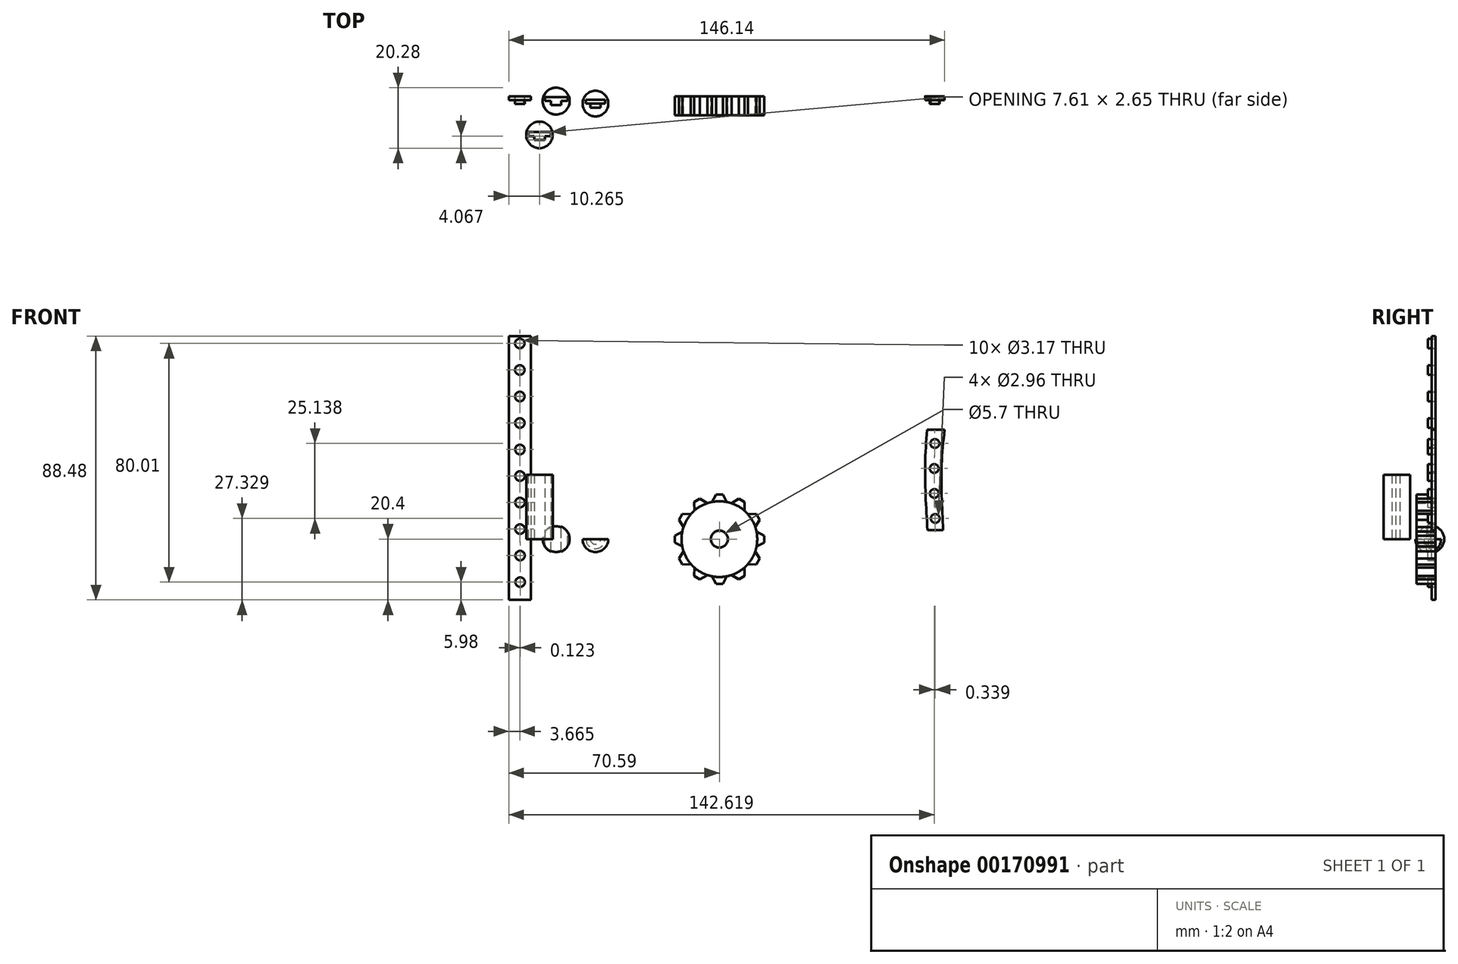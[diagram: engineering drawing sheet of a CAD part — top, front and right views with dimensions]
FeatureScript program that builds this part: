
annotation { "Feature Type Name" : "Feature", "Feature Type Description" : "" }
export const myFeature = defineFeature(function(context is Context, id is Id, definition is map)
    precondition{}
    {
        {
            var Q0;
            Q0=qCreatedBy(makeId("Front.planeOp"),FACE);
            var sketch = newSketch(context, id + "F0", { "sketchPlane" : qUnion([Q0])});
            skLineSegment(sketch, "E0", {"start": v(1.15, 14.98) * mm, "end": v(2.48, 12.45) * mm});
            skLineSegment(sketch, "E1.MirrorCS", {"start": v(-1.15, 14.98) * mm, "end": v(-2.48, 12.45) * mm});
            skLineSegment(sketch, "E2", {"start": v(-1.15, 14.98) * mm, "end": v(1.15, 14.98) * mm});
            skCircle(sketch, "E3", {"center": v(0, 0) * mm, "radius": 2.85 * mm});
            skCircle(sketch, "E4", {"center": v(0, 0) * mm, "radius": 12.7 * mm});
            skLineSegment(sketch, "E5.1.0", {"start": v(-6.5, 13.54) * mm, "end": v(-4.08, 12.03) * mm});
            skLineSegment(sketch, "E5.1.1", {"start": v(-8.48, 12.4) * mm, "end": v(-8.38, 9.54) * mm});
            skLineSegment(sketch, "E5.1.2", {"start": v(-8.48, 12.4) * mm, "end": v(-6.5, 13.54) * mm});
            skLineSegment(sketch, "E5.2.0", {"start": v(-12.4, 8.48) * mm, "end": v(-9.54, 8.38) * mm});
            skLineSegment(sketch, "E5.2.1", {"start": v(-13.54, 6.5) * mm, "end": v(-12.03, 4.08) * mm});
            skLineSegment(sketch, "E5.2.2", {"start": v(-13.54, 6.5) * mm, "end": v(-12.4, 8.48) * mm});
            skLineSegment(sketch, "E5.3.0", {"start": v(-14.98, 1.15) * mm, "end": v(-12.45, 2.48) * mm});
            skLineSegment(sketch, "E5.3.1", {"start": v(-14.98, -1.15) * mm, "end": v(-12.45, -2.48) * mm});
            skLineSegment(sketch, "E5.3.2", {"start": v(-14.98, -1.15) * mm, "end": v(-14.98, 1.15) * mm});
            skLineSegment(sketch, "E5.4.0", {"start": v(-13.54, -6.5) * mm, "end": v(-12.03, -4.08) * mm});
            skLineSegment(sketch, "E5.4.1", {"start": v(-12.4, -8.48) * mm, "end": v(-9.54, -8.38) * mm});
            skLineSegment(sketch, "E5.4.2", {"start": v(-12.4, -8.48) * mm, "end": v(-13.54, -6.5) * mm});
            skLineSegment(sketch, "E5.5.0", {"start": v(-8.48, -12.4) * mm, "end": v(-8.38, -9.54) * mm});
            skLineSegment(sketch, "E5.5.1", {"start": v(-6.5, -13.54) * mm, "end": v(-4.08, -12.03) * mm});
            skLineSegment(sketch, "E5.5.2", {"start": v(-6.5, -13.54) * mm, "end": v(-8.48, -12.4) * mm});
            skLineSegment(sketch, "E5.6.0", {"start": v(-1.15, -14.98) * mm, "end": v(-2.48, -12.45) * mm});
            skLineSegment(sketch, "E5.6.1", {"start": v(1.15, -14.98) * mm, "end": v(2.48, -12.45) * mm});
            skLineSegment(sketch, "E5.6.2", {"start": v(1.15, -14.98) * mm, "end": v(-1.15, -14.98) * mm});
            skLineSegment(sketch, "E5.7.0", {"start": v(6.5, -13.54) * mm, "end": v(4.08, -12.03) * mm});
            skLineSegment(sketch, "E5.7.1", {"start": v(8.48, -12.4) * mm, "end": v(8.38, -9.54) * mm});
            skLineSegment(sketch, "E5.7.2", {"start": v(8.48, -12.4) * mm, "end": v(6.5, -13.54) * mm});
            skLineSegment(sketch, "E5.8.0", {"start": v(12.4, -8.48) * mm, "end": v(9.54, -8.38) * mm});
            skLineSegment(sketch, "E5.8.1", {"start": v(13.54, -6.5) * mm, "end": v(12.03, -4.08) * mm});
            skLineSegment(sketch, "E5.8.2", {"start": v(13.54, -6.5) * mm, "end": v(12.4, -8.48) * mm});
            skLineSegment(sketch, "E5.9.0", {"start": v(14.98, -1.15) * mm, "end": v(12.45, -2.48) * mm});
            skLineSegment(sketch, "E5.9.1", {"start": v(14.98, 1.15) * mm, "end": v(12.45, 2.48) * mm});
            skLineSegment(sketch, "E5.9.2", {"start": v(14.98, 1.15) * mm, "end": v(14.98, -1.15) * mm});
            skLineSegment(sketch, "E5.10.0", {"start": v(13.54, 6.5) * mm, "end": v(12.03, 4.08) * mm});
            skLineSegment(sketch, "E5.10.1", {"start": v(12.4, 8.48) * mm, "end": v(9.54, 8.38) * mm});
            skLineSegment(sketch, "E5.10.2", {"start": v(12.4, 8.48) * mm, "end": v(13.54, 6.5) * mm});
            skLineSegment(sketch, "E5.11.0", {"start": v(8.48, 12.4) * mm, "end": v(8.38, 9.54) * mm});
            skLineSegment(sketch, "E5.11.1", {"start": v(6.5, 13.54) * mm, "end": v(4.08, 12.03) * mm});
            skLineSegment(sketch, "E5.11.2", {"start": v(6.5, 13.54) * mm, "end": v(8.48, 12.4) * mm});
            skLineSegment(sketch, "E6.bottom", {"start": v(48.7, 52.46) * mm, "end": v(58.15, 52.46) * mm});
            skLineSegment(sketch, "E6.top", {"start": v(48.7, 3.3) * mm, "end": v(58.15, 3.3) * mm});
            skLineSegment(sketch, "E6.left", {"start": v(48.7, 52.46) * mm, "end": v(48.7, 3.3) * mm});
            skLineSegment(sketch, "E6.right", {"start": v(58.15, 52.46) * mm, "end": v(58.15, 3.3) * mm});
            skLineSegment(sketch, "E7", {"start": v(53.43, 3.3) * mm, "end": v(53.43, 6.13) * mm});
            skCircle(sketch, "E8", {"center": v(53.43, 6.13) * mm, "radius": 1.38 * mm});
            skFitSpline(sketch, "E9", {"points": [v(69.76, 3.01) * mm, v(69.06, 27.56) * mm, v(71.5, 52.14) * mm], "startDerivative": vector(-2.96, 49.08) * mm, "endDerivative": vector(6.45, 48.4) * mm});
            skFitSpline(sketch, "E10", {"points": [v(74.98, 3.01) * mm, v(74.63, 27.56) * mm, v(77.4, 52.14) * mm], "startDerivative": vector(-1.57, 49.03) * mm, "endDerivative": vector(3.66, 48.45) * mm});
            skLineSegment(sketch, "E11", {"start": v(69.76, 3.01) * mm, "end": v(74.98, 3.01) * mm});
            skCircle(sketch, "E12", {"center": v(72.37, 6.93) * mm, "radius": 1.48 * mm});
            skPoint(sketch, "E12.centerSnap0", {"position": v(72.37, 3.01) * mm});
            skCircle(sketch, "E13.1.0.0", {"center": v(72.07, 15.3) * mm, "radius": 1.48 * mm});
            skCircle(sketch, "E13.2.0.0", {"center": v(72.03, 23.69) * mm, "radius": 1.48 * mm});
            skCircle(sketch, "E13.3.0.0", {"center": v(72.24, 32.07) * mm, "radius": 1.48 * mm});
            skLineSegment(sketch, "E14", {"start": v(69.66, 36.67) * mm, "end": v(75.55, 36.67) * mm});
            skLineSegment(sketch, "E15.bottom", {"start": v(-70.59, 68.08) * mm, "end": v(-63.26, 68.08) * mm});
            skLineSegment(sketch, "E15.top", {"start": v(-70.59, -20.4) * mm, "end": v(-63.26, -20.4) * mm});
            skLineSegment(sketch, "E15.left", {"start": v(-70.59, 68.08) * mm, "end": v(-70.59, -20.4) * mm});
            skLineSegment(sketch, "E15.right", {"start": v(-63.26, 68.08) * mm, "end": v(-63.26, -20.4) * mm});
            skCircle(sketch, "E16", {"center": v(-66.92, 65.6) * mm, "radius": 1.59 * mm});
            skPoint(sketch, "E16.centerSnap0", {"position": v(-66.92, 68.08) * mm});
            skPoint(sketch, "E17.centerSnap0", {"position": v(-66.92, -20.4) * mm});
            skCircle(sketch, "E18.1.0.0", {"center": v(-66.91, 56.7) * mm, "radius": 1.59 * mm});
            skCircle(sketch, "E18.2.0.0", {"center": v(-66.9, 47.81) * mm, "radius": 1.59 * mm});
            skCircle(sketch, "E18.3.0.0", {"center": v(-66.88, 38.92) * mm, "radius": 1.59 * mm});
            skCircle(sketch, "E18.4.0.0", {"center": v(-66.87, 30.03) * mm, "radius": 1.59 * mm});
            skCircle(sketch, "E18.5.0.0", {"center": v(-66.86, 21.14) * mm, "radius": 1.59 * mm});
            skCircle(sketch, "E18.6.0.0", {"center": v(-66.84, 12.25) * mm, "radius": 1.59 * mm});
            skCircle(sketch, "E18.7.0.0", {"center": v(-66.83, 3.36) * mm, "radius": 1.59 * mm});
            skCircle(sketch, "E18.8.0.0", {"center": v(-66.82, -5.53) * mm, "radius": 1.59 * mm});
            skCircle(sketch, "E18.9.0.0", {"center": v(-66.8, -14.42) * mm, "radius": 1.59 * mm});
            skSolve(sketch);
        }
        {
            var Q0;
            Q0=makeQuery(id+"F0.imprint","IMPRINT",FACE,{"disambiguationData":[TD([[makeQuery(id+"F0.imprint","IMPRINT",EDGE,{"derivedFrom":sQuery(id+"F0.wireOp",EDGE,"9e9577b3-fb2f-4fc8-aa35-3dcf2ef7b522")}),-1.0]])]});
            var Q1;
            {var subQ0=sQuery(id+"F0.wireOp",EDGE,"E5.10.0");Q1=makeQuery(id+"F0.imprint","IMPRINT",FACE,{"disambiguationData":[TD([[makeQuery(id+"F0.imprint","IMPRINT",EDGE,{"derivedFrom":subQ0}),-1.0]])]});}
            var Q2;
            {var subQ0=sQuery(id+"F0.wireOp",EDGE,"E5.11.0");Q2=makeQuery(id+"F0.imprint","IMPRINT",FACE,{"disambiguationData":[TD([[makeQuery(id+"F0.imprint","IMPRINT",EDGE,{"derivedFrom":subQ0}),-1.0]])]});}
            var Q3;
            {var subQ0=sQuery(id+"F0.wireOp",EDGE,"E5.2.0");Q3=makeQuery(id+"F0.imprint","IMPRINT",FACE,{"disambiguationData":[TD([[makeQuery(id+"F0.imprint","IMPRINT",EDGE,{"derivedFrom":subQ0}),-1.0]])]});}
            var Q4;
            {var subQ0=sQuery(id+"F0.wireOp",EDGE,"E5.3.0");Q4=makeQuery(id+"F0.imprint","IMPRINT",FACE,{"disambiguationData":[TD([[makeQuery(id+"F0.imprint","IMPRINT",EDGE,{"derivedFrom":subQ0}),-1.0]])]});}
            var Q5;
            {var subQ0=sQuery(id+"F0.wireOp",EDGE,"E5.4.0");Q5=makeQuery(id+"F0.imprint","IMPRINT",FACE,{"disambiguationData":[TD([[makeQuery(id+"F0.imprint","IMPRINT",EDGE,{"derivedFrom":subQ0}),-1.0]])]});}
            var Q6;
            {var subQ0=sQuery(id+"F0.wireOp",EDGE,"E5.5.0");Q6=makeQuery(id+"F0.imprint","IMPRINT",FACE,{"disambiguationData":[TD([[makeQuery(id+"F0.imprint","IMPRINT",EDGE,{"derivedFrom":subQ0}),-1.0]])]});}
            var Q7;
            {var subQ0=sQuery(id+"F0.wireOp",EDGE,"E5.6.0");Q7=makeQuery(id+"F0.imprint","IMPRINT",FACE,{"disambiguationData":[TD([[makeQuery(id+"F0.imprint","IMPRINT",EDGE,{"derivedFrom":subQ0}),-1.0]])]});}
            var Q8;
            {var subQ0=sQuery(id+"F0.wireOp",EDGE,"E5.7.0");Q8=makeQuery(id+"F0.imprint","IMPRINT",FACE,{"disambiguationData":[TD([[makeQuery(id+"F0.imprint","IMPRINT",EDGE,{"derivedFrom":subQ0}),-1.0]])]});}
            var Q9;
            {var subQ0=sQuery(id+"F0.wireOp",EDGE,"E5.8.0");Q9=makeQuery(id+"F0.imprint","IMPRINT",FACE,{"disambiguationData":[TD([[makeQuery(id+"F0.imprint","IMPRINT",EDGE,{"derivedFrom":subQ0}),-1.0]])]});}
            var Q10;
            {var subQ0=sQuery(id+"F0.wireOp",EDGE,"E5.9.0");Q10=makeQuery(id+"F0.imprint","IMPRINT",FACE,{"disambiguationData":[TD([[makeQuery(id+"F0.imprint","IMPRINT",EDGE,{"derivedFrom":subQ0}),-1.0]])]});}
            var Q11;
            {var subQ0=sQuery(id+"F0.wireOp",EDGE,"E0");Q11=makeQuery(id+"F0.imprint","IMPRINT",FACE,{"disambiguationData":[TD([[makeQuery(id+"F0.imprint","IMPRINT",EDGE,{"derivedFrom":subQ0}),-1.0]])]});}
            var Q12;
            {var subQ0=sQuery(id+"F0.wireOp",EDGE,"E5.1.0");Q12=makeQuery(id+"F0.imprint","IMPRINT",FACE,{"disambiguationData":[TD([[makeQuery(id+"F0.imprint","IMPRINT",EDGE,{"derivedFrom":subQ0}),-1.0]])]});}
            extrude(context, id + "F1", {"entities" : qUnion([Q0, Q1, Q2, Q3, Q4, Q5, Q6, Q7, Q8, Q9, Q10, Q11, Q12]), "depth" : 6.35 * mm});
        }
        {
            var Q0;
            Q0=makeQuery(id+"F0.imprint","IMPRINT",FACE,{"disambiguationData":[TD([[makeQuery(id+"F0.imprint","IMPRINT",EDGE,{"derivedFrom":sQuery(id+"F0.wireOp",EDGE,"9e9577b3-fb2f-4fc8-aa35-3dcf2ef7b522")}),-1.0]])]});
            var Q1;
            {var subQ0=sQuery(id+"F0.wireOp",EDGE,"E0");Q1=makeQuery(id+"F0.imprint","IMPRINT",FACE,{"disambiguationData":[TD([[makeQuery(id+"F0.imprint","IMPRINT",EDGE,{"derivedFrom":subQ0}),-1.0]])]});}
            var Q2;
            {var subQ0=sQuery(id+"F0.wireOp",EDGE,"E5.10.0");Q2=makeQuery(id+"F0.imprint","IMPRINT",FACE,{"disambiguationData":[TD([[makeQuery(id+"F0.imprint","IMPRINT",EDGE,{"derivedFrom":subQ0}),-1.0]])]});}
            var Q3;
            {var subQ0=sQuery(id+"F0.wireOp",EDGE,"E5.11.0");Q3=makeQuery(id+"F0.imprint","IMPRINT",FACE,{"disambiguationData":[TD([[makeQuery(id+"F0.imprint","IMPRINT",EDGE,{"derivedFrom":subQ0}),-1.0]])]});}
            var Q4;
            {var subQ0=sQuery(id+"F0.wireOp",EDGE,"E5.1.0");Q4=makeQuery(id+"F0.imprint","IMPRINT",FACE,{"disambiguationData":[TD([[makeQuery(id+"F0.imprint","IMPRINT",EDGE,{"derivedFrom":subQ0}),-1.0]])]});}
            var Q5;
            {var subQ0=sQuery(id+"F0.wireOp",EDGE,"E5.2.0");Q5=makeQuery(id+"F0.imprint","IMPRINT",FACE,{"disambiguationData":[TD([[makeQuery(id+"F0.imprint","IMPRINT",EDGE,{"derivedFrom":subQ0}),-1.0]])]});}
            var Q6;
            {var subQ0=sQuery(id+"F0.wireOp",EDGE,"E5.3.0");Q6=makeQuery(id+"F0.imprint","IMPRINT",FACE,{"disambiguationData":[TD([[makeQuery(id+"F0.imprint","IMPRINT",EDGE,{"derivedFrom":subQ0}),-1.0]])]});}
            var Q7;
            {var subQ0=sQuery(id+"F0.wireOp",EDGE,"E5.4.0");Q7=makeQuery(id+"F0.imprint","IMPRINT",FACE,{"disambiguationData":[TD([[makeQuery(id+"F0.imprint","IMPRINT",EDGE,{"derivedFrom":subQ0}),-1.0]])]});}
            var Q8;
            {var subQ0=sQuery(id+"F0.wireOp",EDGE,"E5.5.0");Q8=makeQuery(id+"F0.imprint","IMPRINT",FACE,{"disambiguationData":[TD([[makeQuery(id+"F0.imprint","IMPRINT",EDGE,{"derivedFrom":subQ0}),-1.0]])]});}
            var Q9;
            {var subQ0=sQuery(id+"F0.wireOp",EDGE,"E5.6.0");Q9=makeQuery(id+"F0.imprint","IMPRINT",FACE,{"disambiguationData":[TD([[makeQuery(id+"F0.imprint","IMPRINT",EDGE,{"derivedFrom":subQ0}),-1.0]])]});}
            var Q10;
            {var subQ0=sQuery(id+"F0.wireOp",EDGE,"E5.7.0");Q10=makeQuery(id+"F0.imprint","IMPRINT",FACE,{"disambiguationData":[TD([[makeQuery(id+"F0.imprint","IMPRINT",EDGE,{"derivedFrom":subQ0}),-1.0]])]});}
            var Q11;
            {var subQ0=sQuery(id+"F0.wireOp",EDGE,"E5.8.0");Q11=makeQuery(id+"F0.imprint","IMPRINT",FACE,{"disambiguationData":[TD([[makeQuery(id+"F0.imprint","IMPRINT",EDGE,{"derivedFrom":subQ0}),-1.0]])]});}
            var Q12;
            {var subQ0=sQuery(id+"F0.wireOp",EDGE,"E5.9.0");Q12=makeQuery(id+"F0.imprint","IMPRINT",FACE,{"disambiguationData":[TD([[makeQuery(id+"F0.imprint","IMPRINT",EDGE,{"derivedFrom":subQ0}),-1.0]])]});}
            var Q13;
            Q13=makeQuery(id+"F0.imprint","IMPRINT",FACE,{"disambiguationData":[TD([[makeQuery(id+"F0.imprint","IMPRINT",EDGE,{"derivedFrom":sQuery(id+"F0.wireOp",EDGE,"E3")}),-1.0]])]});
            extrude(context, id + "F2", {"entities" : qUnion([Q0, Q1, Q2, Q3, Q4, Q5, Q6, Q7, Q8, Q9, Q10, Q11, Q12, Q13]), "depth" : 6.35 * mm});
        }
        {
            var Q0;
            Q0=makeQuery(id+"F0.imprint","IMPRINT",FACE,{"disambiguationData":[TD([[makeQuery(id+"F0.imprint","IMPRINT",EDGE,{"derivedFrom":sQuery(id+"F0.wireOp",EDGE,"E13.5.0.0")}),1.0]])]});
            var Q1;
            Q1=makeQuery(id+"F0.imprint","IMPRINT",FACE,{"disambiguationData":[TD([[makeQuery(id+"F0.imprint","IMPRINT",EDGE,{"derivedFrom":sQuery(id+"F0.wireOp",EDGE,"E13.4.0.0")}),1.0]])]});
            var Q2;
            Q2=makeQuery(id+"F0.imprint","IMPRINT",FACE,{"disambiguationData":[TD([[makeQuery(id+"F0.imprint","IMPRINT",EDGE,{"derivedFrom":sQuery(id+"F0.wireOp",EDGE,"E13.3.0.0")}),1.0]])]});
            var Q3;
            Q3=makeQuery(id+"F0.imprint","IMPRINT",FACE,{"disambiguationData":[TD([[makeQuery(id+"F0.imprint","IMPRINT",EDGE,{"derivedFrom":sQuery(id+"F0.wireOp",EDGE,"E13.2.0.0")}),1.0]])]});
            var Q4;
            Q4=makeQuery(id+"F0.imprint","IMPRINT",FACE,{"disambiguationData":[TD([[makeQuery(id+"F0.imprint","IMPRINT",EDGE,{"derivedFrom":sQuery(id+"F0.wireOp",EDGE,"E13.1.0.0")}),1.0]])]});
            var Q5;
            Q5=makeQuery(id+"F0.imprint","IMPRINT",FACE,{"disambiguationData":[TD([[makeQuery(id+"F0.imprint","IMPRINT",EDGE,{"derivedFrom":sQuery(id+"F0.wireOp",EDGE,"E12")}),1.0]])]});
            extrude(context, id + "F3", {"entities" : qUnion([Q0, Q1, Q2, Q3, Q4, Q5]), "depth" : 2.54 * mm});
        }
        {
            var Q0;
            Q0=makeQuery(id+"F0.imprint","IMPRINT",FACE,{"disambiguationData":[TD([[makeQuery(id+"F0.imprint","IMPRINT",EDGE,{"derivedFrom":sQuery(id+"F0.wireOp",EDGE,"E9")}),-1.0]])]});
            extrude(context, id + "F4", {"entities" : qUnion([Q0]), "depth" : 1.27 * mm});
        }
        {
            var Q0;
            Q0=makeQuery(id+"F0.imprint","IMPRINT",FACE,{"disambiguationData":[TD([[makeQuery(id+"F0.imprint","IMPRINT",EDGE,{"derivedFrom":sQuery(id+"F0.wireOp",EDGE,"E15.bottom")}),-1.0]])]});
            extrude(context, id + "F5", {"entities" : qUnion([Q0]), "depth" : 1.27 * mm});
        }
        {
            var Q0;
            Q0=makeQuery(id+"F0.imprint","IMPRINT",FACE,{"disambiguationData":[TD([[makeQuery(id+"F0.imprint","IMPRINT",EDGE,{"derivedFrom":sQuery(id+"F0.wireOp",EDGE,"E16")}),1.0]])]});
            var Q1;
            Q1=makeQuery(id+"F0.imprint","IMPRINT",FACE,{"disambiguationData":[TD([[makeQuery(id+"F0.imprint","IMPRINT",EDGE,{"derivedFrom":sQuery(id+"F0.wireOp",EDGE,"E18.1.0.0")}),1.0]])]});
            var Q2;
            Q2=makeQuery(id+"F0.imprint","IMPRINT",FACE,{"disambiguationData":[TD([[makeQuery(id+"F0.imprint","IMPRINT",EDGE,{"derivedFrom":sQuery(id+"F0.wireOp",EDGE,"E18.2.0.0")}),1.0]])]});
            var Q3;
            Q3=makeQuery(id+"F0.imprint","IMPRINT",FACE,{"disambiguationData":[TD([[makeQuery(id+"F0.imprint","IMPRINT",EDGE,{"derivedFrom":sQuery(id+"F0.wireOp",EDGE,"E18.3.0.0")}),1.0]])]});
            var Q4;
            Q4=makeQuery(id+"F0.imprint","IMPRINT",FACE,{"disambiguationData":[TD([[makeQuery(id+"F0.imprint","IMPRINT",EDGE,{"derivedFrom":sQuery(id+"F0.wireOp",EDGE,"E18.4.0.0")}),1.0]])]});
            var Q5;
            Q5=makeQuery(id+"F0.imprint","IMPRINT",FACE,{"disambiguationData":[TD([[makeQuery(id+"F0.imprint","IMPRINT",EDGE,{"derivedFrom":sQuery(id+"F0.wireOp",EDGE,"E18.5.0.0")}),1.0]])]});
            var Q6;
            Q6=makeQuery(id+"F0.imprint","IMPRINT",FACE,{"disambiguationData":[TD([[makeQuery(id+"F0.imprint","IMPRINT",EDGE,{"derivedFrom":sQuery(id+"F0.wireOp",EDGE,"E18.6.0.0")}),1.0]])]});
            var Q7;
            Q7=makeQuery(id+"F0.imprint","IMPRINT",FACE,{"disambiguationData":[TD([[makeQuery(id+"F0.imprint","IMPRINT",EDGE,{"derivedFrom":sQuery(id+"F0.wireOp",EDGE,"E18.7.0.0")}),1.0]])]});
            var Q8;
            Q8=makeQuery(id+"F0.imprint","IMPRINT",FACE,{"disambiguationData":[TD([[makeQuery(id+"F0.imprint","IMPRINT",EDGE,{"derivedFrom":sQuery(id+"F0.wireOp",EDGE,"E18.9.0.0")}),1.0]])]});
            var Q9;
            Q9=makeQuery(id+"F0.imprint","IMPRINT",FACE,{"disambiguationData":[TD([[makeQuery(id+"F0.imprint","IMPRINT",EDGE,{"derivedFrom":sQuery(id+"F0.wireOp",EDGE,"E18.8.0.0")}),1.0]])]});
            extrude(context, id + "F6", {"entities" : qUnion([Q0, Q1, Q2, Q3, Q4, Q5, Q6, Q7, Q8, Q9]), "depth" : 2.54 * mm});
        }
        {
            var Q0;
            Q0=qCreatedBy(makeId("Top.planeOp"),FACE);
            var sketch = newSketch(context, id + "F7", { "sketchPlane" : qUnion([Q0])});
            skLineSegment(sketch, "E19", {"start": v(-54.7, -0.24) * mm, "end": v(-58.55, -0.24) * mm});
            skLineSegment(sketch, "E20", {"start": v(-58.55, -1.58) * mm, "end": v(-56.41, -1.58) * mm});
            skLineSegment(sketch, "E21", {"start": v(-56.41, -1.58) * mm, "end": v(-56.41, -2.96) * mm});
            skLineSegment(sketch, "E22", {"start": v(-56.41, -2.96) * mm, "end": v(-54.7, -2.96) * mm});
            skLineSegment(sketch, "E23", {"start": v(-58.55, -0.24) * mm, "end": v(-58.55, -1.58) * mm});
            skArc(sketch, "E24", {"start": v(-54.7, 2.91) * mm, "mid": v(-59.22, -1.6) * mm, "end": v(-54.7, -6.11) * mm});
            skLineSegment(sketch, "E25", {"start": v(-41.54, -1.1) * mm, "end": v(-38.35, -1.1) * mm});
            skLineSegment(sketch, "E26", {"start": v(-38.35, -1.1) * mm, "end": v(-38.35, -2.47) * mm});
            skLineSegment(sketch, "E27", {"start": v(-38.35, -2.47) * mm, "end": v(-39.8, -2.47) * mm});
            skLineSegment(sketch, "E28", {"start": v(-39.8, -2.47) * mm, "end": v(-39.8, -3.84) * mm});
            skLineSegment(sketch, "E29", {"start": v(-39.8, -3.84) * mm, "end": v(-41.54, -3.84) * mm});
            skLineSegment(sketch, "E30", {"start": v(-41.54, 1.85) * mm, "end": v(-41.54, -1.1) * mm});
            skLineSegment(sketch, "E31.trimOffspring", {"start": v(-41.54, -3.84) * mm, "end": v(-41.54, -6.99) * mm});
            skLineSegment(sketch, "E32", {"start": v(-41.54, -7.92) * mm, "end": v(-41.54, 3) * mm, "construction": true});
            skLineSegment(sketch, "E33.MirrorCS", {"start": v(-53, -1.58) * mm, "end": v(-53, -2.96) * mm});
            skLineSegment(sketch, "E34.MirrorCS", {"start": v(-50.86, -0.24) * mm, "end": v(-50.86, -1.58) * mm});
            skLineSegment(sketch, "E35.MirrorCS", {"start": v(-50.86, -1.58) * mm, "end": v(-53, -1.58) * mm});
            skLineSegment(sketch, "E36.MirrorCS", {"start": v(-53, -2.96) * mm, "end": v(-54.7, -2.96) * mm});
            skLineSegment(sketch, "E37.MirrorCS", {"start": v(-54.7, -0.24) * mm, "end": v(-50.86, -0.24) * mm});
            skLineSegment(sketch, "E38", {"start": v(-54.7, 0.25) * mm, "end": v(-54.7, -3.39) * mm, "construction": true});
            skLineSegment(sketch, "E39", {"start": v(-64.13, -11.98) * mm, "end": v(-56.52, -11.98) * mm});
            skLineSegment(sketch, "E40", {"start": v(-56.52, -11.98) * mm, "end": v(-56.52, -13.37) * mm});
            skLineSegment(sketch, "E41", {"start": v(-56.52, -13.37) * mm, "end": v(-58.46, -13.37) * mm});
            skLineSegment(sketch, "E42", {"start": v(-58.46, -13.37) * mm, "end": v(-58.46, -14.63) * mm});
            skLineSegment(sketch, "E43", {"start": v(-58.46, -14.63) * mm, "end": v(-62.04, -14.63) * mm});
            skLineSegment(sketch, "E44", {"start": v(-62.04, -14.63) * mm, "end": v(-62.04, -13.39) * mm});
            skLineSegment(sketch, "E45", {"start": v(-62.04, -13.39) * mm, "end": v(-64.13, -13.39) * mm});
            skLineSegment(sketch, "E46", {"start": v(-64.13, -13.39) * mm, "end": v(-64.13, -11.98) * mm});
            skCircle(sketch, "E47", {"center": v(-60.33, -12.93) * mm, "radius": 4.45 * mm});
            skLineSegment(sketch, "E48", {"start": v(-60.33, -7.85) * mm, "end": v(-60.33, -18.28) * mm, "construction": true});
            skCircle(sketch, "E49", {"center": v(-41.54, -2.45) * mm, "radius": 4.3 * mm});
            skLineSegment(sketch, "E50", {"start": v(-54.7, 2.91) * mm, "end": v(-54.7, -6.11) * mm});
            skSolve(sketch);
        }
        {
            var Q0;
            Q0=makeQuery(id+"F7.imprint","IMPRINT",FACE,{"disambiguationData":[TD([[makeQuery(id+"F7.imprint","IMPRINT",EDGE,{"derivedFrom":sQuery(id+"F7.wireOp",EDGE,"E39")}),1.0]])]});
            extrude(context, id + "F8", {"entities" : qUnion([Q0]), "depth" : 21.59 * mm});
        }
        {
            var Q0;
            Q0=makeQuery(id+"F7.imprint","IMPRINT",FACE,{"disambiguationData":[TD([[makeQuery(id+"F7.imprint","IMPRINT",EDGE,{"derivedFrom":sQuery(id+"F7.wireOp",EDGE,"E25")}),1.0]])]});
            var Q1;
            Q1=sQuery(id+"F7.wireOp",EDGE,"E32");
            revolve(context, id + "F9", {"entities" : qUnion([Q0]), "axis" : qUnion([Q1]), "revolveType" : RevolveType.ONE_DIRECTION, "angle" : 180 * degree});
        }
        {
            var Q0;
            {var subQ2=sQuery(id+"F7.wireOp",EDGE,"E19");Q0=makeQuery(id+"F7.imprint","IMPRINT",FACE,{"disambiguationData":[TD([[makeQuery(id+"F7.imprint","IMPRINT",EDGE,{"derivedFrom":subQ2}),-1.0]])]});}
            var Q1;
            {var subQ1=sQuery(id+"F7.wireOp",EDGE,"E19");Q1=makeQuery(id+"F7.imprint","IMPRINT",FACE,{"disambiguationData":[TD([[makeQuery(id+"F7.imprint","IMPRINT",EDGE,{"derivedFrom":subQ1}),1.0]])]});}
            var Q2;
            Q2=sQuery(id+"F7.wireOp",EDGE,"E50");
            revolve(context, id + "F10", {"entities" : qUnion([Q0, Q1]), "axis" : qUnion([Q2]), "revolveType" : RevolveType.FULL});
        }
        {
            var Q0;
            Q0=makeQuery(id+"F7.imprint","IMPRINT",FACE,{"disambiguationData":[TD([[makeQuery(id+"F7.imprint","IMPRINT",EDGE,{"derivedFrom":sQuery(id+"F7.wireOp",EDGE,"E33.MirrorCS")}),-1.0]])]});
            var Q1;
            {var subQ1=sQuery(id+"F7.wireOp",EDGE,"E19");Q1=makeQuery(id+"F7.imprint","IMPRINT",FACE,{"disambiguationData":[TD([[makeQuery(id+"F7.imprint","IMPRINT",EDGE,{"derivedFrom":subQ1}),1.0]])]});}
            extrude(context, id + "F11", {"entities" : qUnion([Q0, Q1]), "operationType" : NewBodyOperationType.REMOVE, "oppositeDirection" : true, "depth" : 25.4 * mm, "hasSecondDirection" : true, "secondDirectionOppositeDirection" : false, "secondDirectionDepth" : 25.4 * mm});
        }
    });
